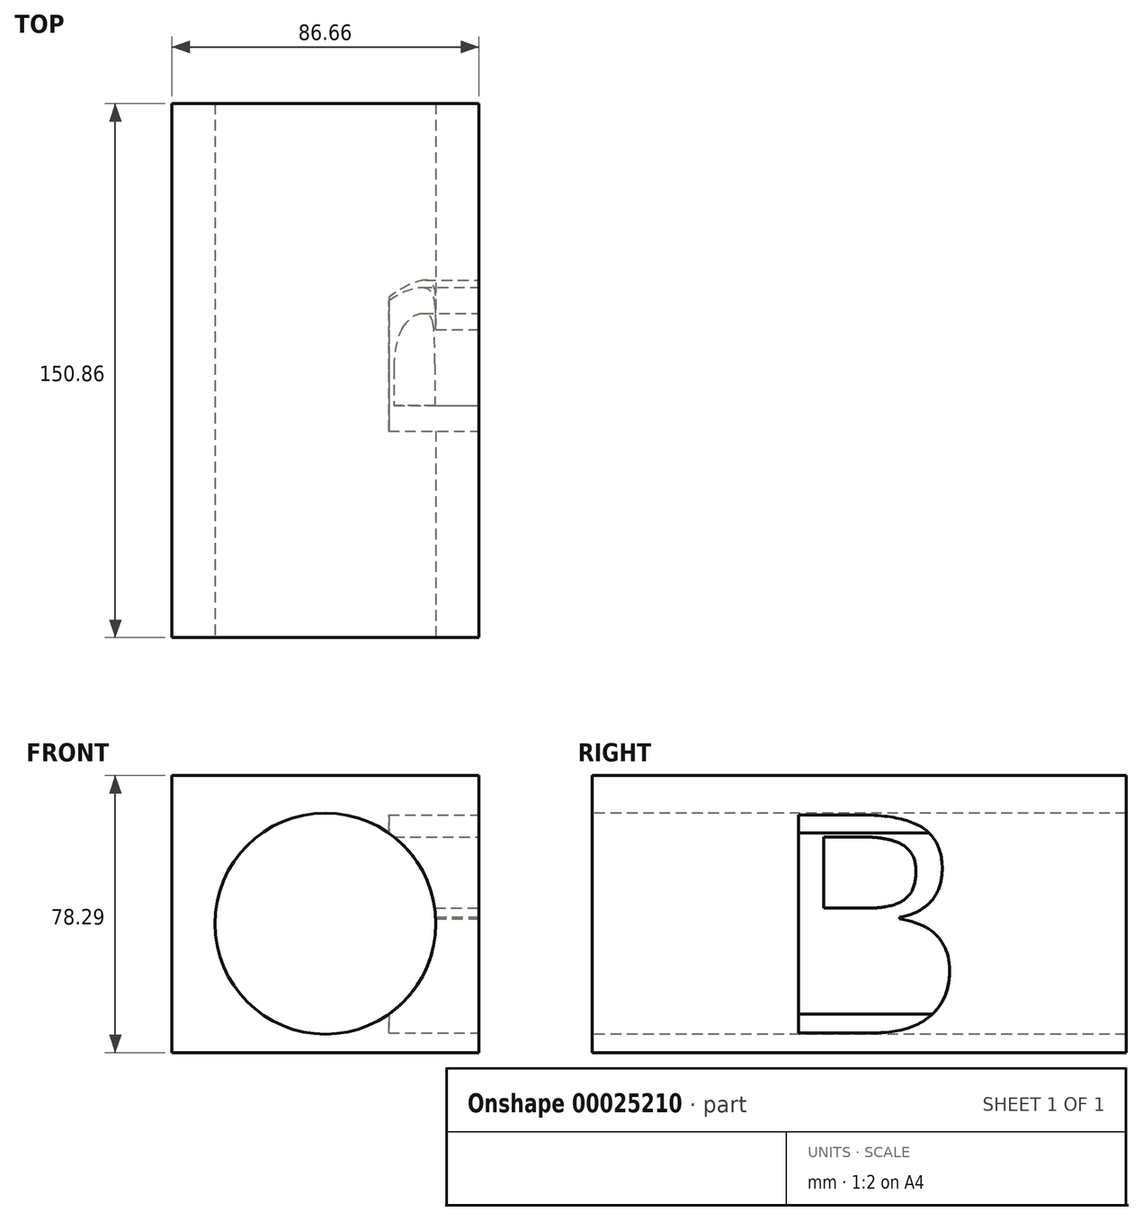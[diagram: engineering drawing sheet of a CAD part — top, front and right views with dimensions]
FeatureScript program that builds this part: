
annotation { "Feature Type Name" : "Feature", "Feature Type Description" : "" }
export const myFeature = defineFeature(function(context is Context, id is Id, definition is map)
    precondition{}
    {
        {
            var Q0;
            Q0=qCreatedBy(makeId("Top.planeOp"),FACE);
            var sketch = newSketch(context, id + "F0", { "sketchPlane" : qUnion([Q0])});
            skLineSegment(sketch, "E0.rect.bottom", {"start": v(43.33, -75.43) * mm, "end": v(-43.33, -75.43) * mm});
            skLineSegment(sketch, "E0.rect.top", {"start": v(43.33, 75.43) * mm, "end": v(-43.33, 75.43) * mm});
            skLineSegment(sketch, "E0.rect.left", {"start": v(43.33, -75.43) * mm, "end": v(43.33, 75.43) * mm});
            skLineSegment(sketch, "E0.rect.right", {"start": v(-43.33, -75.43) * mm, "end": v(-43.33, 75.43) * mm});
            skPoint(sketch, "E0.rect.middle", {"position": v(0, 0) * mm});
            skSolve(sketch);
        }
        {
            var Q0;
            Q0=makeQuery(id+"F0.imprint","IMPRINT",FACE,{"disambiguationData":[TD([[makeQuery(id+"F0.imprint","IMPRINT",EDGE,{"derivedFrom":sQuery(id+"F0.wireOp",EDGE,"E0.rect.bottom")}),-1.0]])]});
            extrude(context, id + "F1", {"entities" : qUnion([Q0]), "depth" : 78.3 * mm});
        }
        {
            var Q0;
            Q0=makeQuery(id+"F1.opExtrude","SWEPT_FACE",FACE,{"disambiguationData":[OSD([sQuery(id+"F0.wireOp",EDGE,"E0.rect.bottom")])]});
            var sketch = newSketch(context, id + "F2", { "sketchPlane" : qUnion([Q0])});
            skCircle(sketch, "E1", {"center": v(0, 36.43) * mm, "radius": 31.23 * mm});
            skSolve(sketch);
        }
        {
            var Q0;
            Q0=makeQuery(id+"F2.imprint","IMPRINT",FACE,{"disambiguationData":[TD([[makeQuery(id+"F2.imprint","IMPRINT",EDGE,{"derivedFrom":sQuery(id+"F2.wireOp",EDGE,"E1")}),1.0]])]});
            extrude(context, id + "F3", {"entities" : qUnion([Q0]), "operationType" : NewBodyOperationType.REMOVE, "oppositeDirection" : true, "depth" : 219.92 * mm});
        }
        {
            var Q0;
            Q0=makeQuery(id+"F1.opExtrude","SWEPT_FACE",FACE,{"disambiguationData":[OSD([sQuery(id+"F0.wireOp",EDGE,"E0.rect.left")])]});
            var sketch = newSketch(context, id + "F4", { "sketchPlane" : qUnion([Q0])});
            skText(sketch, "E2", { "text": "B", "fontName": "OpenSans-Regular.ttf"});
            const initialGuessF4  = {"E2": [-0.02556, 0.00558, 1, 0, 0.06208]};
            skSetInitialGuess(sketch, initialGuessF4);
            skSolve(sketch);
        }
        {
            var Q0;
            Q0=makeQuery(id+"F4.imprint","IMPRINT",FACE,{"disambiguationData":[TD([[makeQuery(id+"F4.imprint","IMPRINT",EDGE,{"derivedFrom":sQuery(id+"F4.wireOp",EDGE,"E2.sketch_text.stroke-18")}),1.0]])]});
            var Q1;
            Q1=makeQuery(id+"F4.imprint","IMPRINT",FACE,{"disambiguationData":[TD([[makeQuery(id+"F4.imprint","IMPRINT",EDGE,{"derivedFrom":sQuery(id+"F4.wireOp",EDGE,"E2.sketch_text.stroke-0")}),-1.0]])]});
            extrude(context, id + "F5", {"entities" : qUnion([Q0, Q1]), "operationType" : NewBodyOperationType.REMOVE, "oppositeDirection" : true, "depth" : 25.4 * mm});
        }
    });
